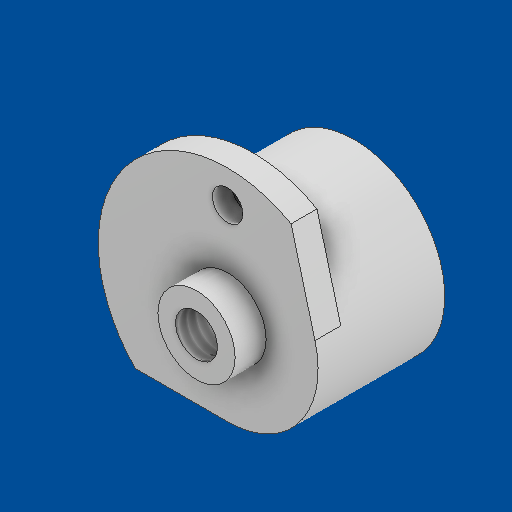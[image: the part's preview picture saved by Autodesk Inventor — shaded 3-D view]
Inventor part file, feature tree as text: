
AUTODESK INVENTOR PART (.ipt)
format: ipt  version: 2025 (Build 290162000, 162)  size: 146,944 bytes
history: native  units: in
note: dims shown in document units (in); Inventor stores cm internally (conversion verified against a paired STEP export)
features: direct_edit x1, hole x1, sketch x1, other x1
ambient origin geometry x8: Origin, YZ Plane, XZ Plane, XY Plane, X Axis, Y Axis, Z Axis, Center Point
bodies: Solid1 (feature_tree), Body1 (feature_tree)
feature tree (4):
  direct_edit  "Direct Edit1"
  hole  "Hole1"  [1 undecoded]
  sketch  "Sketch1"  dims[d0=0.0394in d1=0.0787in d2=0.1276in d3=0.3937in d4=0.1575in d5=0.0787in d6=90.0deg d7=0.315in d8=0.8108in]
  other  "Size1"
note: 1 required parameter value undecoded (feature->parameter linkage not recoverable at this tier; creation-order binding heuristic only, values carry confidence <= 0.55)
